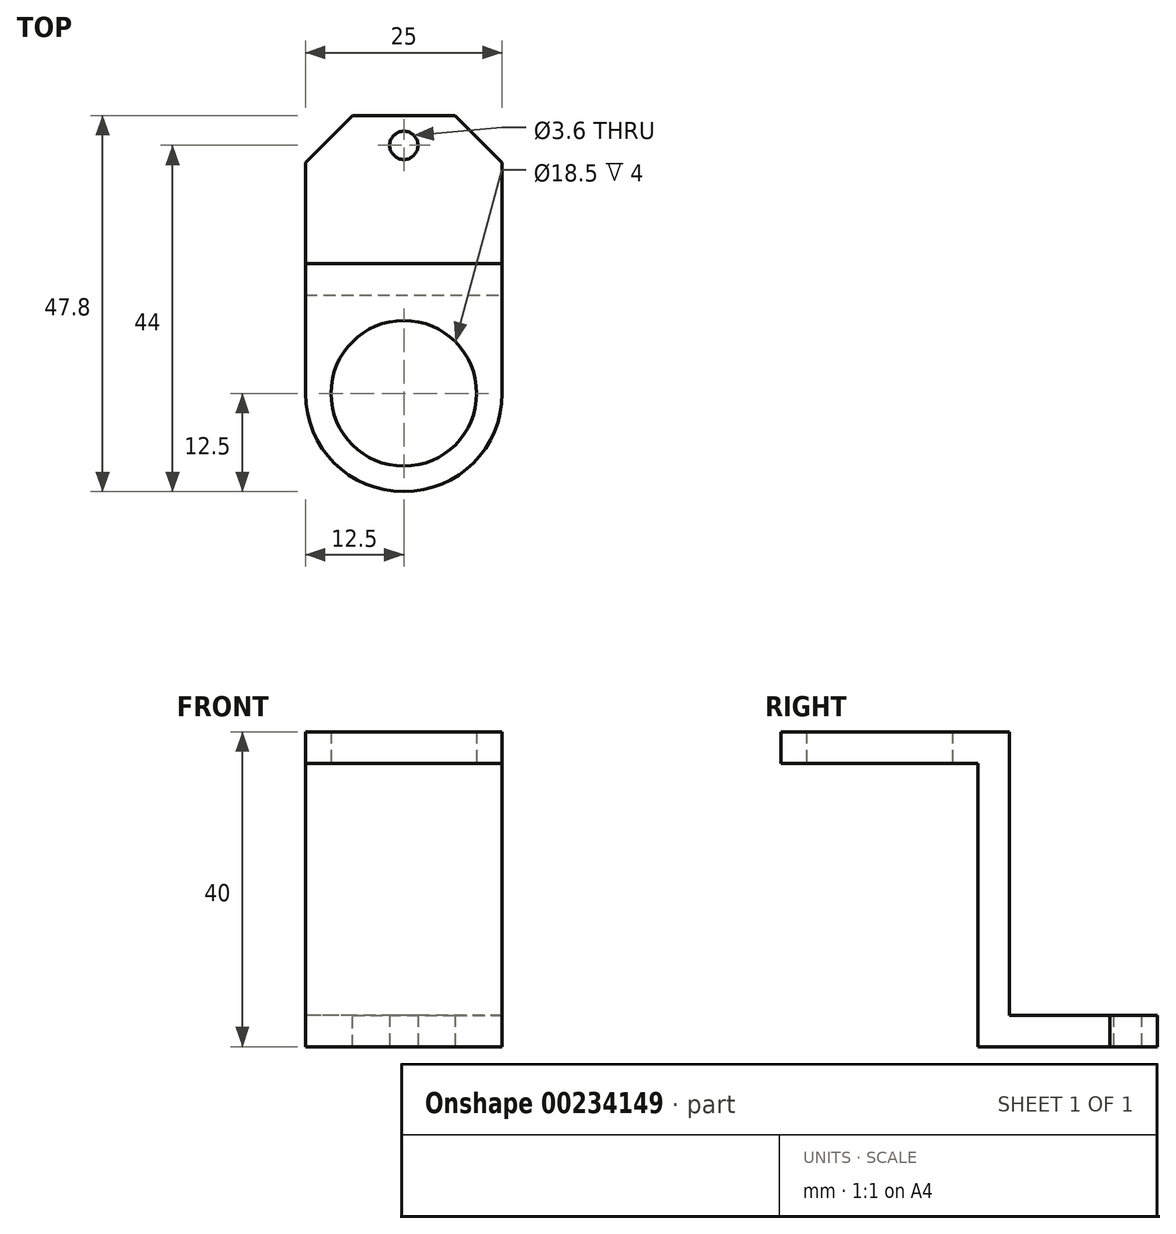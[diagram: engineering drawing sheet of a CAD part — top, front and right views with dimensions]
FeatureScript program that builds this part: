
annotation { "Feature Type Name" : "Feature", "Feature Type Description" : "" }
export const myFeature = defineFeature(function(context is Context, id is Id, definition is map)
    precondition{}
    {
        {
            var Q0;
            Q0=qCreatedBy(makeId("Top.planeOp"),FACE);
            var sketch = newSketch(context, id + "F0", { "sketchPlane" : qUnion([Q0])});
            skLineSegment(sketch, "E0.bottom", {"start": v(-12.5, 0) * mm, "end": v(12.5, 0) * mm});
            skLineSegment(sketch, "E0.top", {"start": v(-12.5, -22.8) * mm, "end": v(12.5, -22.8) * mm});
            skLineSegment(sketch, "E0.left", {"start": v(-12.5, 0) * mm, "end": v(-12.5, -22.8) * mm});
            skLineSegment(sketch, "E0.right", {"start": v(12.5, 0) * mm, "end": v(12.5, -22.8) * mm});
            skCircle(sketch, "E1", {"center": v(0, -3.8) * mm, "radius": 1.8 * mm});
            skPoint(sketch, "E1.centerSnap0", {"position": v(0, 0) * mm});
            skPoint(sketch, "E2", {"position": v(12.5, -11.4) * mm});
            skLineSegment(sketch, "E3", {"start": v(12.5, -18.8) * mm, "end": v(-12.5, -18.8) * mm});
            skSolve(sketch);
        }
        {
            var Q0;
            {var subQ1=sQuery(id+"F0.wireOp",EDGE,"E0.bottom");Q0=makeQuery(id+"F0.imprint","IMPRINT",FACE,{"disambiguationData":[TD([[makeQuery(id+"F0.imprint","IMPRINT",EDGE,{"derivedFrom":subQ1}),-1.0]])]});}
            extrude(context, id + "F1", {"entities" : qUnion([Q0]), "depth" : 4 * mm});
        }
        {
            var Q0;
            {var subQ0=sQuery(id+"F0.wireOp",EDGE,"E0.top");Q0=makeQuery(id+"F0.imprint","IMPRINT",FACE,{"disambiguationData":[TD([[makeQuery(id+"F0.imprint","IMPRINT",EDGE,{"derivedFrom":subQ0}),1.0]])]});}
            extrude(context, id + "F2", {"entities" : qUnion([Q0]), "operationType" : NewBodyOperationType.ADD, "depth" : 40 * mm});
        }
        {
            var Q0;
            Q0=makeQuery(id+"F2.opExtrude","SWEPT_FACE",FACE,{"disambiguationData":[OSD([sQuery(id+"F0.wireOp",EDGE,"E0.top")])]});
            var sketch = newSketch(context, id + "F3", { "sketchPlane" : qUnion([Q0])});
            skLineSegment(sketch, "E4", {"start": v(12.5, 36) * mm, "end": v(-12.5, 36) * mm});
            skSolve(sketch);
        }
        {
            var Q0;
            {var subQ0=sQuery(id+"F3.wireOp",EDGE,"E4");Q0=makeQuery(id+"F3.imprint","IMPRINT",FACE,{"disambiguationData":[TD([[makeQuery(id+"F3.imprint","IMPRINT",EDGE,{"derivedFrom":subQ0}),-1.0]])]});}
            extrude(context, id + "F4", {"entities" : qUnion([Q0]), "operationType" : NewBodyOperationType.ADD, "depth" : 25 * mm});
        }
        {
            var Q0;
            Q0=makeQuery(id+"F4.opExtrude","SWEPT_FACE",FACE,{"disambiguationData":[OSD([sQuery(id+"F3.wireOp",EDGE,"E4")])]});
            var sketch = newSketch(context, id + "F5", { "sketchPlane" : qUnion([Q0])});
            skCircle(sketch, "E5", {"center": v(0, 35.3) * mm, "radius": 9.25 * mm});
            skPoint(sketch, "E5.centerSnap0", {"position": v(-12.5, 35.3) * mm});
            skPoint(sketch, "E5.centerSnap1", {"position": v(0, 47.8) * mm});
            skSolve(sketch);
        }
        {
            var Q0;
            Q0=makeQuery(id+"F5.imprint","IMPRINT",FACE,{"disambiguationData":[TD([[makeQuery(id+"F5.imprint","IMPRINT",EDGE,{"derivedFrom":sQuery(id+"F5.wireOp",EDGE,"E5")}),1.0]])]});
            extrude(context, id + "F6", {"entities" : qUnion([Q0]), "operationType" : NewBodyOperationType.REMOVE, "endBound" : BoundingType.UP_TO_NEXT, "oppositeDirection" : true, "depth" : 25 * mm});
        }
        {
            var Q0;
            Q0=makeQuery(id+"F4.opExtrude","CAP_EDGE",EDGE,{"disambiguationData":[OSD([sQuery(id+"F0.wireOp",EDGE,"E0.top"),sQuery(id+"F0.wireOp",EDGE,"E0.right")])],"isStart":false});
            var Q1;
            Q1=makeQuery(id+"F4.opExtrude","CAP_EDGE",EDGE,{"disambiguationData":[OSD([sQuery(id+"F0.wireOp",EDGE,"E0.top"),sQuery(id+"F0.wireOp",EDGE,"E0.left")])],"isStart":false});
            fillet(context, id + "F7", {"entities" : qUnion([Q0, Q1]), "radius" : 12.5 * mm, "tangentPropagation" : true, "allowEdgeOverflow" : false});
        }
        {
            var Q0;
            Q0=makeQuery(id+"F1.opExtrude","SWEPT_EDGE",EDGE,{"disambiguationData":[OSD([sQuery(id+"F0.wireOp",EDGE,"E0.bottom"),sQuery(id+"F0.wireOp",EDGE,"E0.right")])]});
            var Q1;
            Q1=makeQuery(id+"F1.opExtrude","SWEPT_EDGE",EDGE,{"disambiguationData":[OSD([sQuery(id+"F0.wireOp",EDGE,"E0.bottom"),sQuery(id+"F0.wireOp",EDGE,"E0.left")])]});
            chamfer(context, id + "F8", {"entities" : qUnion([Q0, Q1]), "width" : 6 * mm, "tangentPropagation" : true});
        }
    });
